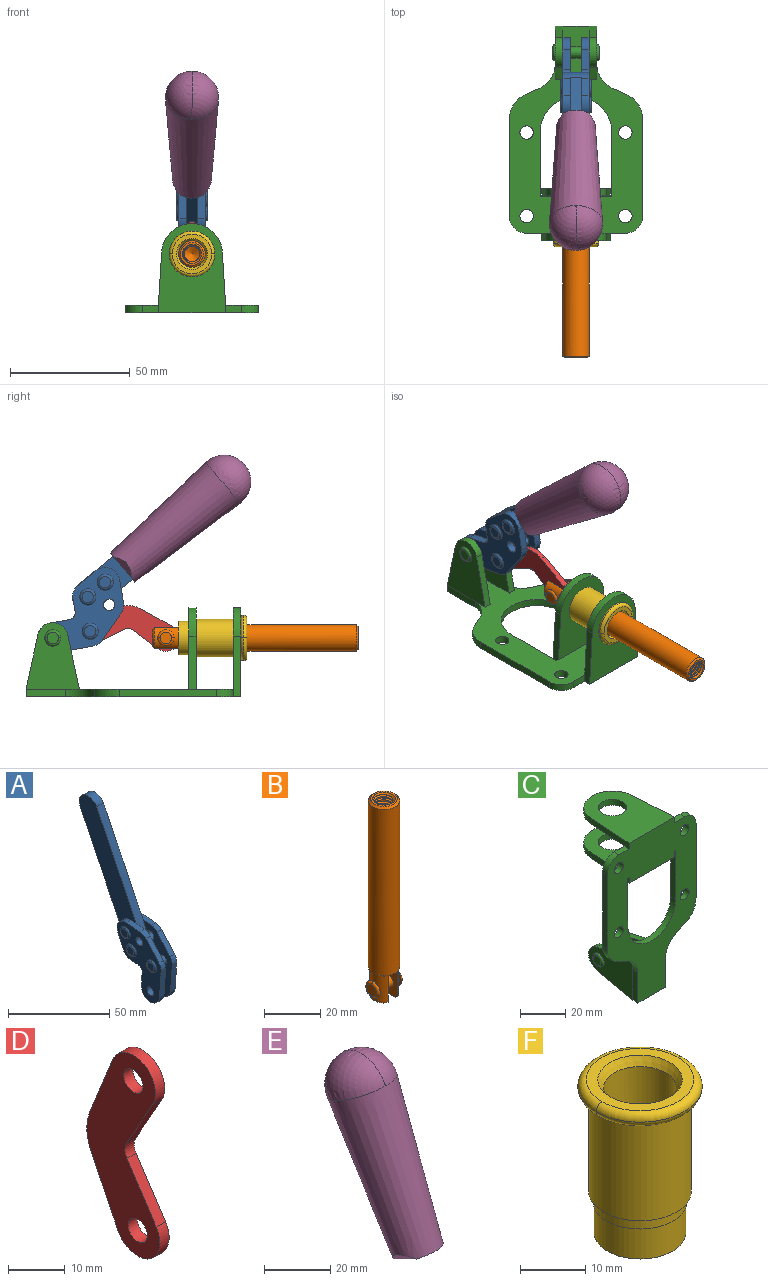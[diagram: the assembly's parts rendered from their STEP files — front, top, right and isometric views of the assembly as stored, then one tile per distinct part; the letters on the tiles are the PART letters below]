
ASSEMBLY  parts=6 mates=6
PART A: 59 faces, bbox 12.9x60.2x99.6 mm
  f0: torus R=2.39mm, axis (-1,0,0), area 14.9mm2, adj f20,f43,f51
  f1: torus R=2.39mm, axis (-1,0,0), area 14.9mm2, adj f19,f42,f51
  f2: torus R=2.39mm, axis (-1,0,0), area 14.9mm2, adj f18,f35,f51
  f3: torus R=2.39mm, axis (-1,0,0), area 14.9mm2, adj f14,f17,f23
  f4: torus R=2.39mm, axis (-1,0,0), area 14.9mm2, adj f13,f16,f23
  f5: torus R=2.39mm, axis (-1,0,0), area 14.9mm2, adj f12,f15,f23
  f6: cylinder r=2.39mm len=4.78mm, axis (1,0,0), area 46.5mm2, adj f48,f50,f51
  f7: cylinder r=2.39mm len=4.78mm, axis (1,0,0), area 46.5mm2, adj f50,f51
  f8: cylinder r=6.35mm len=12.68mm, axis (1,0,0), area 61.8mm2, adj f38,f39,f50,f51
  f9: cylinder r=2.39mm len=4.78mm, axis (-1,0,0), area 70.5mm2, adj f46,f50
  f10: cylinder r=2.39mm len=4.78mm, axis (-1,0,0), area 46.5mm2, adj f23,f45,f46
  f11: cylinder r=2.39mm len=4.78mm, axis (-1,0,0), area 46.5mm2, adj f23,f46
  f12: plane 4.78x4.78mm, normal (1,0,0), area 17.9mm2, adj f5,f15
  f13: plane 4.78x4.78mm, normal (1,0,0), area 17.9mm2, adj f4,f16
  f14: plane 4.78x4.78mm, normal (1,0,0), area 17.9mm2, adj f3,f17
  f15: torus R=2.39mm, axis (-1,0,0), area 14.9mm2, adj f5,f12,f23
  f16: torus R=2.39mm, axis (-1,0,0), area 14.9mm2, adj f4,f13,f23
  f17: torus R=2.39mm, axis (-1,0,0), area 14.9mm2, adj f3,f14,f23
  f18: plane 4.78x4.78mm, normal (-1,0,0), area 17.9mm2, adj f2,f35
  f19: plane 4.78x4.78mm, normal (-1,0,0), area 17.9mm2, adj f1,f42
  f20: plane 4.78x4.78mm, normal (-1,0,0), area 17.9mm2, adj f0,f43
  f21: plane 2.26x0.2mm, normal (1,0,0), area 0.2mm2, adj f31,f44
  f22: plane 2.26x0.2mm, normal (-1,0,0), area 0.2mm2, adj f41,f44
  f23: plane 39.37x30.77mm, normal (1,0,0), area 565.5mm2, adj f3,f4,f5,f10,f11,f15,f16,f17
  f24: cylinder r=6.1mm len=4.15mm, axis (-1,0,0), area 14.7mm2, adj f23,f25,f32,f46
  f25: plane 10.25x9.01mm, normal (0,-0.75,0.66), area 42.3mm2, adj f23,f24,f26,f46
  f26: cylinder r=6.35mm len=4.64mm, axis (-1,0,0), area 15.6mm2, adj f23,f25,f27,f46
  f27: plane 15.84x3.1mm, normal (0,-1,-0.07), area 49.2mm2, adj f23,f26,f28,f46
  f28: cylinder r=6.35mm len=12.68mm, axis (-1,0,0), area 61.8mm2, adj f23,f27,f29,f46
  f29: plane 8.11x3.1mm, normal (0,1,0.07), area 25.2mm2, adj f23,f28,f30,f46
  f30: cylinder r=3.05mm len=3.25mm, axis (-1,0,0), area 14.8mm2, adj f23,f29,f31,f46
  f31: plane 5.99x3.1mm, normal (0,0.07,-1), area 18.6mm2, adj f21,f23,f30,f44,f46
  f32: plane 9.5x3.1mm, normal (0,-0.07,1), area 29.5mm2, adj f23,f24,f33,f46,f47
  f33: cylinder r=6.1mm len=8.63mm, axis (-1,0,0), area 39.1mm2, adj f23,f32,f34,f47
  f34: plane 8.65x3.96mm, normal (0,0.91,-0.42), area 29.5mm2, adj f23,f33,f44,f47
  f35: torus R=2.39mm, axis (-1,0,0), area 14.9mm2, adj f2,f18,f51
  f36: plane 10.25x9.01mm, normal (0,-0.75,0.66), area 42.3mm2, adj f37,f49,f50,f51
  f37: cylinder r=6.35mm len=4.64mm, axis (1,0,0), area 15.6mm2, adj f36,f38,f50,f51
  f38: plane 15.84x3.1mm, normal (0,-1,-0.07), area 49.2mm2, adj f8,f37,f50,f51
  f39: plane 8.11x3.1mm, normal (0,1,0.07), area 25.2mm2, adj f8,f40,f50,f51
  f40: cylinder r=3.05mm len=3.25mm, axis (1,0,0), area 14.8mm2, adj f39,f41,f50,f51
  f41: plane 5.99x3.1mm, normal (0,0.07,-1), area 18.6mm2, adj f22,f40,f44,f50,f51
  f42: torus R=2.39mm, axis (-1,0,0), area 14.9mm2, adj f1,f19,f51
  f43: torus R=2.39mm, axis (-1,0,0), area 14.9mm2, adj f0,f20,f51
  f44: cylinder r=6.35mm len=12.12mm, axis (-1,0,0), area 128.9mm2, adj f21,f22,f23,f31,f34,f41,f46,f47
  f45: plane 2.65x1.35mm, normal (1,0,0), area 1mm2, adj f10,f55
  f46: plane 39.08x20.42mm, normal (-1,0,0), area 412.5mm2, adj f9,f10,f11,f24,f25,f26,f27,f28
  f47: plane 77.62x39.82mm, normal (1,0,0), area 850mm2, adj f32,f33,f34,f44,f53,f54,f55
  f48: plane 2.65x1.35mm, normal (-1,0,0), area 1mm2, adj f6,f55
  f49: cylinder r=6.1mm len=4.15mm, axis (1,0,0), area 14.7mm2, adj f36,f50,f51,f56
  f50: plane 39.08x20.42mm, normal (1,0,0), area 412.5mm2, adj f6,f7,f8,f9,f36,f37,f38,f39
  f51: plane 39.37x30.77mm, normal (-1,0,0), area 565.5mm2, adj f0,f1,f2,f6,f7,f8,f35,f36
  f52: plane 8.65x3.96mm, normal (0,0.91,-0.42), area 29.5mm2, adj f44,f51,f57,f58
  f53: plane 68.49x33.4mm, normal (0,0.9,-0.44), area 358.1mm2, adj f44,f47,f54,f58
  f54: cylinder r=6.35mm len=12.06mm, axis (1,0,0), area 93.7mm2, adj f47,f53,f55,f58
  f55: plane 68.49x33.4mm, normal (0,-0.9,0.44), area 358.1mm2, adj f44,f45,f46,f47,f48,f50,f54,f58
  f56: plane 9.5x3.1mm, normal (0,-0.07,1), area 29.5mm2, adj f49,f50,f51,f57,f58
  f57: cylinder r=6.1mm len=8.63mm, axis (1,0,0), area 39.1mm2, adj f51,f52,f56,f58
  f58: plane 77.62x39.82mm, normal (-1,0,0), area 850mm2, adj f44,f52,f53,f54,f55,f56,f57
PART B: 48 faces, bbox 12.6x11.1x86.1 mm
  f0: torus R=2.41mm, axis (-1,0,0), area 15mm2, adj f30,f32,f34
  f1: torus R=2.41mm, axis (-1,0,0), area 15mm2, adj f29,f31,f33
  f2: cylinder r=5.54mm len=72.39mm, axis (0,0,1), area 2518.5mm2, adj f3,f4,f42,f43
  f3: cone r=5.54mm half-angle=45deg, axis (0,0,1), area 7.6mm2, adj f2,f5,f41
  f4: cone r=5.54mm half-angle=45deg, axis (0,0,-1), area 34.9mm2, adj f2,f39
  f5: cylinder r=5.08mm len=11.48mm, axis (0,0,1), area 108.3mm2, adj f3,f7,f8,f41
  f6: cylinder r=2.41mm len=4.83mm, axis (-1,0,0), area 71.2mm2, adj f40,f41
  f7: cylinder r=2.41mm len=4.83mm, axis (-1,0,0), area 7.6mm2, adj f5,f34
  f8: cone r=5.08mm half-angle=45deg, axis (0,0,1), area 10.6mm2, adj f5,f37,f41
  f9: cone r=3.98mm half-angle=45deg, axis (0,0,1), area 17.6mm2, adj f27,f39,f45,f46,f47
  f10: cylinder r=2.41mm len=4.83mm, axis (-1,0,0), area 7.6mm2, adj f33,f38
  f11: cylinder r=3.2mm len=6.4mm, axis (0,0,1), area 78.4mm2, adj f12,f28,f44,f45,f47
  f12: cylinder r=3.2mm len=6.4mm, axis (0,0,1), area 10.5mm2, adj f11,f13,f45,f47
  f13: cylinder r=3.2mm len=6.4mm, axis (0,0,1), area 10.5mm2, adj f12,f14,f45,f47
  f14: cylinder r=3.2mm len=6.4mm, axis (0,0,1), area 10.5mm2, adj f13,f15,f45,f47
  f15: cylinder r=3.2mm len=6.4mm, axis (0,0,1), area 10.5mm2, adj f14,f16,f45,f47
  f16: cylinder r=3.2mm len=6.4mm, axis (0,0,1), area 10.5mm2, adj f15,f17,f45,f47
  f17: cylinder r=3.2mm len=6.4mm, axis (0,0,1), area 10.5mm2, adj f16,f18,f45,f47
  f18: cylinder r=3.2mm len=6.4mm, axis (0,0,1), area 10.5mm2, adj f17,f19,f45,f47
  f19: cylinder r=3.2mm len=6.4mm, axis (0,0,1), area 10.5mm2, adj f18,f20,f45,f47
  f20: cylinder r=3.2mm len=6.4mm, axis (0,0,1), area 10.5mm2, adj f19,f21,f45,f47
  f21: cylinder r=3.2mm len=6.4mm, axis (0,0,1), area 10.5mm2, adj f20,f22,f45,f47
  f22: cylinder r=3.2mm len=6.4mm, axis (0,0,1), area 10.5mm2, adj f21,f23,f45,f47
  f23: cylinder r=3.2mm len=6.4mm, axis (0,0,1), area 10.5mm2, adj f22,f24,f45,f47
  f24: cylinder r=3.2mm len=6.4mm, axis (0,0,1), area 10.5mm2, adj f23,f25,f45,f47
  f25: cylinder r=3.2mm len=6.4mm, axis (0,0,1), area 10.5mm2, adj f24,f26,f45,f47
  f26: cylinder r=3.2mm len=6.4mm, axis (0,0,1), area 10.5mm2, adj f25,f27,f45,f47
  f27: cylinder r=3.2mm len=6.4mm, axis (0,0,1), area 7.4mm2, adj f9,f26,f45,f47
  f28: cone r=3.2mm half-angle=60deg, axis (0,0,1), area 37.2mm2, adj f11
  f29: plane 4.83x4.83mm, normal (-1,0,0), area 18.3mm2, adj f1,f31
  f30: plane 4.83x4.83mm, normal (1,0,0), area 18.3mm2, adj f0,f32
  f31: torus R=2.41mm, axis (-1,0,0), area 15mm2, adj f1,f29,f33
  f32: torus R=2.41mm, axis (-1,0,0), area 15mm2, adj f0,f30,f34
  f33: plane 6.83x6.83mm, normal (1,0,0), area 18.3mm2, adj f1,f10,f31
  f34: plane 6.83x6.83mm, normal (-1,0,0), area 18.3mm2, adj f0,f7,f32
  f35: cone r=5.08mm half-angle=45deg, axis (0,0,1), area 10.6mm2, adj f36,f38,f40
  f36: plane 7.25x1.97mm, normal (0,0,-1), area 10mm2, adj f35,f40
  f37: plane 7.25x1.97mm, normal (0,0,-1), area 10mm2, adj f8,f41
  f38: cylinder r=5.08mm len=11.48mm, axis (0,0,1), area 108.3mm2, adj f10,f35,f40,f42
  f39: plane 9.55x9.55mm, normal (0,0,1), area 22mm2, adj f4,f9
  f40: plane 12.76x10.09mm, normal (1,0,0), area 95.7mm2, adj f6,f35,f36,f38,f42,f43
  f41: plane 12.76x10.09mm, normal (-1,0,0), area 95.7mm2, adj f3,f5,f6,f8,f37,f43
  f42: cone r=5.54mm half-angle=45deg, axis (0,0,1), area 7.6mm2, adj f2,f38,f40
  f43: plane 11.07x4.7mm, normal (0,0,-1), area 50.4mm2, adj f2,f40,f41
  f44: plane 0.89x0.62mm, normal (-1,0,0), area 0.3mm2, adj f11,f45,f46,f47
  f45: bspline ~24.8x7.63mm, area 266.6mm2, adj f9,f11,f12,f13,f14,f15,f16,f17
  f46: bspline ~24.87x7.63mm, area 73.6mm2, adj f9,f44,f45,f47
  f47: bspline ~24.98x7.63mm, area 272.5mm2, adj f9,f11,f12,f13,f14,f15,f16,f17
PART C: 55 faces, bbox 55.7x37.4x89.8 mm
  f0: torus R=2.41mm, axis (-1,0,0), area 15mm2, adj f11,f15,f25
  f1: torus R=2.41mm, axis (-1,0,0), area 15mm2, adj f10,f12,f22
  f2: cylinder r=2.78mm len=5.56mm, axis (0,-1,0), area 54.2mm2, adj f30,f54
  f3: cylinder r=14.99mm len=29.97mm, axis (0,-1,0), area 145.9mm2, adj f30,f49,f53,f54
  f4: cylinder r=2.78mm len=5.56mm, axis (0,-1,0), area 54.2mm2, adj f30,f54
  f5: cylinder r=2.78mm len=5.56mm, axis (0,-1,0), area 54.2mm2, adj f30,f54
  f6: cylinder r=2.78mm len=5.56mm, axis (0,-1,0), area 54.2mm2, adj f30,f54
  f7: cylinder r=6.35mm len=12.7mm, axis (0,0,1), area 123.6mm2, adj f27,f51
  f8: cylinder r=6.35mm len=12.7mm, axis (0,0,-1), area 124.7mm2, adj f21,f35
  f9: cylinder r=2.41mm len=11.18mm, axis (-1,0,0), area 169.4mm2, adj f16,f19
  f10: plane 4.83x4.83mm, normal (1,0,0), area 18.3mm2, adj f1,f12
  f11: plane 4.83x4.83mm, normal (-1,0,0), area 18.3mm2, adj f0,f15
  f12: torus R=2.41mm, axis (-1,0,0), area 15mm2, adj f1,f10,f22
  f13: cylinder r=6.35mm len=12.41mm, axis (1,0,0), area 53.4mm2, adj f18,f19,f22,f23
  f14: cylinder r=6.35mm len=12.41mm, axis (-1,0,0), area 53.4mm2, adj f16,f17,f24,f25
  f15: torus R=2.41mm, axis (-1,0,0), area 15mm2, adj f0,f11,f25
  f16: plane 27.86x22.35mm, normal (1,0,0), area 425.4mm2, adj f9,f14,f17,f24,f30
  f17: plane 22.86x4.97mm, normal (0,0.21,0.98), area 72.5mm2, adj f14,f16,f25,f30
  f18: plane 22.86x4.97mm, normal (0,0.21,0.98), area 72.5mm2, adj f13,f19,f22,f30
  f19: plane 27.86x22.35mm, normal (-1,0,0), area 425.4mm2, adj f9,f13,f18,f23,f30
  f20: cylinder r=12.7mm len=25.35mm, axis (0,0,-1), area 119.8mm2, adj f21,f34,f35,f36
  f21: plane 34.21x28.07mm, normal (0,0,-1), area 702.4mm2, adj f8,f20,f30,f34,f36
  f22: plane 27.96x22.45mm, normal (1,0,0), area 407.2mm2, adj f1,f12,f13,f18,f23,f30,f42,f43
  f23: plane 22.86x4.97mm, normal (0,0.21,-0.98), area 72.5mm2, adj f13,f19,f22,f44
  f24: plane 22.86x4.97mm, normal (0,0.21,-0.98), area 72.5mm2, adj f14,f16,f25,f44
  f25: plane 27.86x22.35mm, normal (-1,0,0), area 407.1mm2, adj f0,f14,f15,f17,f24,f30,f45,f46
  f26: plane 3.1x0.95mm, normal (0,0,-1), area 2.7mm2, adj f30,f49,f50,f54
  f27: plane 34.21x28.07mm, normal (0,0,1), area 702.4mm2, adj f7,f28,f30,f50,f52
  f28: cylinder r=12.7mm len=25.35mm, axis (0,0,1), area 118.8mm2, adj f27,f50,f51,f52
  f29: plane 3.1x0.95mm, normal (0,0,-1), area 2.7mm2, adj f30,f52,f53,f54
  f30: plane 86.54x55.63mm, normal (0,1,0), area 2362.9mm2, adj f2,f3,f4,f5,f6,f16,f17,f18
  f31: plane 40.56x3.1mm, normal (-1,0,0), area 125.7mm2, adj f30,f32,f48,f54
  f32: cylinder r=7.11mm len=7.11mm, axis (0,-1,0), area 34.6mm2, adj f30,f31,f33,f54
  f33: plane 6.67x3.1mm, normal (0,0,1), area 20.4mm2, adj f30,f32,f34,f54
  f34: plane 25.39x3.13mm, normal (-1,0.06,0), area 79.5mm2, adj f20,f21,f33,f35,f54
  f35: plane 37.31x28.45mm, normal (0,0,1), area 789.9mm2, adj f8,f20,f34,f36,f54
  f36: plane 25.39x3.13mm, normal (1,0.06,0), area 79.5mm2, adj f20,f21,f35,f37,f54
  f37: plane 6.67x3.1mm, normal (0,0,1), area 20.4mm2, adj f30,f36,f38,f54
  f38: cylinder r=7.11mm len=7.11mm, axis (0,-1,0), area 34.6mm2, adj f30,f37,f39,f54
  f39: plane 40.56x3.1mm, normal (1,0,0), area 125.7mm2, adj f30,f38,f40,f54
  f40: cylinder r=11.18mm len=10.16mm, axis (0,-1,0), area 39.5mm2, adj f30,f39,f41,f54
  f41: plane 6.09x3.1mm, normal (0.42,0,-0.91), area 20.8mm2, adj f30,f40,f42,f54
  f42: cylinder r=11.18mm len=9.41mm, axis (0,-1,0), area 37.2mm2, adj f22,f30,f41,f43,f54
  f43: plane 16.5x3.1mm, normal (1,0,0), area 51.1mm2, adj f22,f42,f44,f54
  f44: plane 17.37x3.1mm, normal (0,0,-1), area 53.8mm2, adj f23,f24,f30,f43,f45,f54
  f45: plane 16.5x3.1mm, normal (-1,0,0), area 51.1mm2, adj f25,f44,f46,f54
  f46: cylinder r=11.18mm len=9.41mm, axis (0,-1,0), area 37.2mm2, adj f25,f30,f45,f47,f54
  f47: plane 6.09x3.1mm, normal (-0.42,0,-0.91), area 20.8mm2, adj f30,f46,f48,f54
  f48: cylinder r=11.18mm len=10.16mm, axis (0,-1,0), area 39.5mm2, adj f30,f31,f47,f54
  f49: plane 26.54x3.1mm, normal (-1,0,0), area 82.3mm2, adj f3,f26,f30,f54
  f50: plane 25.39x3.1mm, normal (1,0.06,0), area 78.8mm2, adj f26,f27,f28,f51,f54
  f51: plane 37.31x28.45mm, normal (0,0,-1), area 789.9mm2, adj f7,f28,f50,f52,f54
  f52: plane 25.39x3.1mm, normal (-1,0.06,0), area 78.8mm2, adj f27,f28,f29,f51,f54
  f53: plane 26.54x3.1mm, normal (1,0,0), area 82.3mm2, adj f3,f29,f30,f54
  f54: plane 89.66x55.63mm, normal (0,-1,0), area 2678.5mm2, adj f2,f3,f4,f5,f6,f26,f29,f31
PART D: 12 faces, bbox 2.3x18.2x42.8 mm
  f0: cylinder r=2.4mm len=4.8mm, axis (1,0,0), area 34.9mm2, adj f4,f11
  f1: cylinder r=10.41mm len=8.47mm, axis (1,0,0), area 20.2mm2, adj f4,f9,f10,f11
  f2: cylinder r=3.05mm len=3.16mm, axis (1,0,0), area 7.7mm2, adj f4,f6,f7,f11
  f3: cylinder r=2.4mm len=4.8mm, axis (1,0,0), area 34.9mm2, adj f4,f11
  f4: plane 42.81x18.23mm, normal (-1,0,0), area 414.1mm2, adj f0,f1,f2,f3,f5,f6,f7,f8
  f5: cylinder r=5.54mm len=10.67mm, axis (1,0,0), area 41.8mm2, adj f4,f6,f10,f11
  f6: plane 11.66x6.53mm, normal (0,-0.87,-0.49), area 30.9mm2, adj f2,f4,f5,f11
  f7: plane 11.17x7.33mm, normal (0,-0.84,0.55), area 30.9mm2, adj f2,f4,f8,f11
  f8: cylinder r=5.54mm len=10.51mm, axis (1,0,0), area 41.8mm2, adj f4,f7,f9,f11
  f9: plane 13.67x6.67mm, normal (0,0.9,-0.44), area 35.1mm2, adj f1,f4,f8,f11
  f10: plane 14.1x5.7mm, normal (0,0.93,0.37), area 35.1mm2, adj f1,f4,f5,f11
  f11: plane 42.81x18.23mm, normal (1,0,0), area 414.1mm2, adj f0,f1,f2,f3,f5,f6,f7,f8
PART E: 11 faces, bbox 22.3x42.6x64.5 mm
  f0: sphere r=11.13mm, area 411.4mm2, adj f1,f8
  f1: cone r=11.11mm half-angle=3.3deg, axis (0,0.44,0.9), area 3251.8mm2, adj f0,f7,f8,f9,f10
  f2: cylinder r=6.16mm len=11.7mm, axis (1,0,0), area 89.5mm2, adj f3,f4,f5,f6
  f3: plane 60.23x36.75mm, normal (-1,0,0), area 763.6mm2, adj f2,f4,f6,f10
  f4: plane 51.37x25.05mm, normal (0,0.9,-0.44), area 264.2mm2, adj f2,f3,f5,f10
  f5: plane 60.23x36.75mm, normal (1,0,0), area 763.6mm2, adj f2,f4,f6,f10
  f6: plane 51.37x25.05mm, normal (0,-0.9,0.44), area 264.2mm2, adj f2,f3,f5,f10
  f7: plane 9.95x5.95mm, normal (0.71,-0.31,-0.64), area 25.8mm2, adj f1,f10
  f8: sphere r=11.13mm, area 411.4mm2, adj f0,f1
  f9: plane 9.95x5.95mm, normal (-0.71,-0.31,-0.64), area 25.8mm2, adj f1,f10
  f10: plane 14.27x11.38mm, normal (0,-0.44,-0.9), area 106.7mm2, adj f1,f3,f4,f5,f6,f7,f9
PART F: 15 faces, bbox 20.6x20.6x28.7 mm
  f0: torus R=8.26mm, axis (0,0,1), area 56.8mm2, adj f1,f10,f12
  f1: torus R=8.26mm, axis (0,0,1), area 56.8mm2, adj f0,f6,f13
  f2: cylinder r=5.59mm len=25.91mm, axis (0,0,1), area 909.6mm2, adj f3,f4
  f3: cone r=6.86mm half-angle=45deg, axis (0,0,-1), area 70.2mm2, adj f2,f14
  f4: cone r=6.47mm half-angle=30deg, axis (0,0,1), area 66.7mm2, adj f2,f13
  f5: cylinder r=7.04mm len=14.07mm, axis (0,0,1), area 252.6mm2, adj f11,f14
  f6: torus R=8.26mm, axis (0,0,1), area 56.8mm2, adj f1,f12,f13
  f7: cylinder r=7.16mm len=14.33mm, axis (0,0,1), area 91.5mm2, adj f9,f11
  f8: cylinder r=7.86mm len=18.42mm, axis (0,0,1), area 909.6mm2, adj f9,f10
  f9: plane 15.72x15.72mm, normal (0,0,-1), area 33mm2, adj f7,f8
  f10: plane 16.51x16.51mm, normal (0,0,-1), area 19.9mm2, adj f0,f8,f12
  f11: plane 14.33x14.33mm, normal (0,0,-1), area 5.7mm2, adj f5,f7
  f12: torus R=8.26mm, axis (0,0,1), area 56.8mm2, adj f0,f6,f10
  f13: plane 16.51x16.51mm, normal (0,0,1), area 82.7mm2, adj f1,f4,f6
  f14: plane 14.07x14.07mm, normal (0,0,-1), area 7.8mm2, adj f3,f5
PLACE A rot(axis=(1,0,0),75.8deg) t=(0,4.09,8.61)mm
PLACE B rot(axis=(1,0,0),90deg) t=(0,9.46,0)mm
PLACE C rot(axis=(1,0,0),90deg) t=(0,9.14,0)mm fixed
PLACE D rot(axis=(1,0,0),97.1deg) t=(0,12.37,2.09)mm
PLACE E rot(axis=(1,0,0),75.8deg) t=(0,4.09,8.61)mm
PLACE F rot(axis=(1,0,0),90deg) t=(0,9.14,0)mm
MATE cylindrical D.f3 <-> A.f4  axis (1,0,0) through (0,25.61,27.42)mm
MATE revolute C.f0 <-> A.f7  axis (-1,0,0) through (0,41.23,24.61)mm
MATE revolute B.f6 <-> D.f5  axis (-1,0,0) through (0,-6.02,24.61)mm
MATE fastened E.f2 <-> A.f54  axis (1,0,0) through (0,-31.61,90.91)mm
MATE slider B.f2 <-> C.f7  axis (0,-1,0) through (0,-49.32,24.61)mm
MATE fastened F.f0 <-> C.f7  axis (0,1,0) through (0,-37.25,24.61)mm
